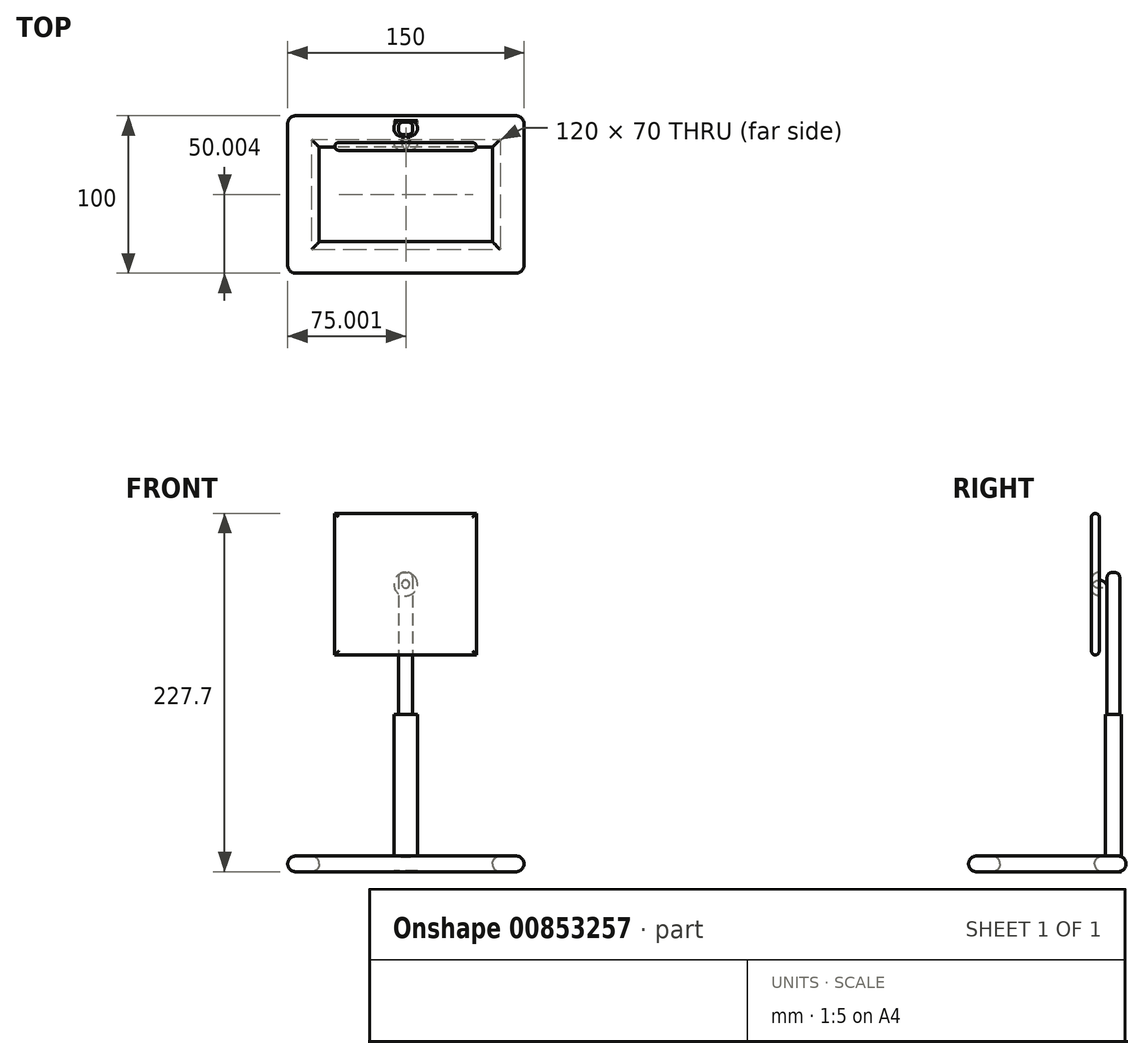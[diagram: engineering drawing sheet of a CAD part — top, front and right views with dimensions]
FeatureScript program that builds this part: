
annotation { "Feature Type Name" : "Feature", "Feature Type Description" : "" }
export const myFeature = defineFeature(function(context is Context, id is Id, definition is map)
    precondition{}
    {
        {
            var Q0;
            Q0=qCreatedBy(makeId("Top.planeOp"),FACE);
            var sketch = newSketch(context, id + "F0", { "sketchPlane" : qUnion([Q0])});
            skLineSegment(sketch, "E0", {"start": v(-74.85, -45.82) * mm, "end": v(75.15, -45.82) * mm});
            skLineSegment(sketch, "E1", {"start": v(-74.85, -45.82) * mm, "end": v(-74.85, 54.18) * mm});
            skLineSegment(sketch, "E2", {"start": v(-74.85, 54.18) * mm, "end": v(75.15, 54.18) * mm});
            skLineSegment(sketch, "E3", {"start": v(75.15, 54.18) * mm, "end": v(75.15, -45.82) * mm});
            skLineSegment(sketch, "E4", {"start": v(-54.85, 34.18) * mm, "end": v(-54.85, -25.82) * mm});
            skLineSegment(sketch, "E5", {"start": v(55.15, 34.18) * mm, "end": v(55.15, -25.82) * mm});
            skLineSegment(sketch, "E6", {"start": v(-54.85, 34.18) * mm, "end": v(55.15, 34.18) * mm});
            skLineSegment(sketch, "E7.trimOffspring", {"start": v(-54.85, -25.82) * mm, "end": v(55.15, -25.82) * mm});
            skLineSegment(sketch, "E8", {"start": v(0, 0) * mm, "end": v(0.15, 111.46) * mm, "construction": true});
            skPoint(sketch, "E8.endSnap0", {"position": v(0.15, 54.18) * mm});
            skLineSegment(sketch, "E9", {"start": v(-7.43, 51.18) * mm, "end": v(7.57, 51.18) * mm});
            skLineSegment(sketch, "E10", {"start": v(-7.43, 51.18) * mm, "end": v(-7.43, 41.18) * mm});
            skLineSegment(sketch, "E11", {"start": v(-7.43, 41.18) * mm, "end": v(7.57, 41.18) * mm});
            skLineSegment(sketch, "E12", {"start": v(7.57, 41.18) * mm, "end": v(7.57, 51.18) * mm});
            skSolve(sketch);
        }
        {
            var Q0;
            Q0=qSketchRegion(id+"F0",true);
            extrude(context, id + "F1", {"entities" : qUnion([Q0]), "depth" : 10 * mm, "offsetDistance" : 25 * mm});
        }
        {
            var Q0;
            Q0=makeQuery(id+"F1.opExtrude","CAP_EDGE",EDGE,{"disambiguationData":[OSD([sQuery(id+"F0.wireOp",EDGE,"E2")])],"isStart":false});
            var Q1;
            Q1=makeQuery(id+"F1.opExtrude","CAP_EDGE",EDGE,{"disambiguationData":[OSD([sQuery(id+"F0.wireOp",EDGE,"E1")])],"isStart":false});
            var Q2;
            Q2=makeQuery(id+"F1.opExtrude","CAP_EDGE",EDGE,{"disambiguationData":[OSD([sQuery(id+"F0.wireOp",EDGE,"E0")])],"isStart":false});
            var Q3;
            Q3=makeQuery(id+"F1.opExtrude","CAP_EDGE",EDGE,{"disambiguationData":[OSD([sQuery(id+"F0.wireOp",EDGE,"E3")])],"isStart":false});
            var Q4;
            Q4=makeQuery(id+"F1.opExtrude","CAP_EDGE",EDGE,{"disambiguationData":[OSD([sQuery(id+"F0.wireOp",EDGE,"E6")])],"isStart":false});
            var Q5;
            Q5=makeQuery(id+"F1.opExtrude","CAP_EDGE",EDGE,{"disambiguationData":[OSD([sQuery(id+"F0.wireOp",EDGE,"E4")])],"isStart":false});
            var Q6;
            Q6=makeQuery(id+"F1.opExtrude","CAP_EDGE",EDGE,{"disambiguationData":[OSD([sQuery(id+"F0.wireOp",EDGE,"E5")])],"isStart":false});
            var Q7;
            Q7=makeQuery(id+"F1.opExtrude","CAP_EDGE",EDGE,{"disambiguationData":[OSD([sQuery(id+"F0.wireOp",EDGE,"E7.trimOffspring")])],"isStart":false});
            fillet(context, id + "F2", {"entities" : qUnion([Q0, Q1, Q2, Q3, Q4, Q5, Q6, Q7]), "radius" : 5 * mm, "tangentPropagation" : true, "allowEdgeOverflow" : false});
        }
        {
            var Q0;
            Q0=makeQuery(id+"F1.opExtrude","CAP_EDGE",EDGE,{"disambiguationData":[OSD([sQuery(id+"F0.wireOp",EDGE,"E0")])],"isStart":true});
            fillet(context, id + "F3", {"entities" : qUnion([Q0]), "radius" : 5 * mm, "tangentPropagation" : true, "allowEdgeOverflow" : false});
        }
        {
            var Q0;
            Q0=makeQuery(id+"F1.opExtrude","CAP_EDGE",EDGE,{"disambiguationData":[OSD([sQuery(id+"F0.wireOp",EDGE,"E2")])],"isStart":true});
            fillet(context, id + "F4", {"entities" : qUnion([Q0]), "radius" : 5 * mm, "tangentPropagation" : true, "allowEdgeOverflow" : false});
        }
        {
            var Q0;
            Q0=makeQuery(id+"F1.opExtrude","CAP_EDGE",EDGE,{"disambiguationData":[OSD([sQuery(id+"F0.wireOp",EDGE,"E5")])],"isStart":true});
            var Q1;
            Q1=makeQuery(id+"F1.opExtrude","CAP_EDGE",EDGE,{"disambiguationData":[OSD([sQuery(id+"F0.wireOp",EDGE,"E6")])],"isStart":true});
            var Q2;
            Q2=makeQuery(id+"F1.opExtrude","CAP_EDGE",EDGE,{"disambiguationData":[OSD([sQuery(id+"F0.wireOp",EDGE,"E7.trimOffspring")])],"isStart":true});
            var Q3;
            Q3=makeQuery(id+"F1.opExtrude","CAP_EDGE",EDGE,{"disambiguationData":[OSD([sQuery(id+"F0.wireOp",EDGE,"E4")])],"isStart":true});
            fillet(context, id + "F5", {"entities" : qUnion([Q0, Q1, Q2, Q3]), "radius" : 5 * mm, "tangentPropagation" : true, "allowEdgeOverflow" : false});
        }
        {
            var Q0;
            Q0=makeQuery(id+"F2.opFillet","BLEND_EDGE",EDGE,{"blendedFrom":[makeQuery(id+"F1.opExtrude","CAP_EDGE",EDGE,{"disambiguationData":[OSD([sQuery(id+"F0.wireOp",EDGE,"E0")])],"isStart":false}),makeQuery(id+"F1.opExtrude","CAP_EDGE",EDGE,{"disambiguationData":[OSD([sQuery(id+"F0.wireOp",EDGE,"E3")])],"isStart":false})],"blendedInto":[]});
            fillet(context, id + "F6", {"entities" : qUnion([Q0]), "radius" : 5 * mm, "tangentPropagation" : true, "allowEdgeOverflow" : false});
        }
        {
            var Q0;
            Q0=makeQuery(id+"F2.opFillet","BLEND_EDGE",EDGE,{"blendedFrom":[makeQuery(id+"F1.opExtrude","CAP_EDGE",EDGE,{"disambiguationData":[OSD([sQuery(id+"F0.wireOp",EDGE,"E1")])],"isStart":false}),makeQuery(id+"F1.opExtrude","CAP_EDGE",EDGE,{"disambiguationData":[OSD([sQuery(id+"F0.wireOp",EDGE,"E2")])],"isStart":false})],"blendedInto":[]});
            fillet(context, id + "F7", {"entities" : qUnion([Q0]), "radius" : 5 * mm, "tangentPropagation" : true, "allowEdgeOverflow" : false});
        }
        {
            var Q0;
            Q0=makeQuery(id+"F0.imprint","IMPRINT",FACE,{"disambiguationData":[TD([[makeQuery(id+"F0.imprint","IMPRINT",EDGE,{"derivedFrom":sQuery(id+"F0.wireOp",EDGE,"E9")}),-1.0]])]});
            extrude(context, id + "F8", {"entities" : qUnion([Q0]), "operationType" : NewBodyOperationType.ADD, "depth" : 100 * mm, "offsetDistance" : 25 * mm});
        }
        {
            var Q0;
            Q0=makeQuery(id+"F8.opExtrude","SWEPT_EDGE",EDGE,{"disambiguationData":[OSD([sQuery(id+"F0.wireOp",EDGE,"E11"),sQuery(id+"F0.wireOp",EDGE,"E12")])]});
            var Q1;
            {var subQ0=sQuery(id+"F0.wireOp",EDGE,"E9");var subQ1=sQuery(id+"F0.wireOp",EDGE,"E12");Q1=makeQuery(id+"F8.boolean.opBoolean","SPLIT",EDGE,{"disambiguationData":[TD([makeQuery(id+"F8.opExtrude","CAP_FACE",FACE,{"disambiguationData":[OSD([subQ0,sQuery(id+"F0.wireOp",EDGE,"E10"),sQuery(id+"F0.wireOp",EDGE,"E11"),subQ1])],"isStart":false})])],"derivedFrom":makeQuery(id+"F8.opExtrude","SWEPT_EDGE",EDGE,{"disambiguationData":[OSD([subQ0,subQ1])]})});}
            var Q2;
            Q2=makeQuery(id+"F8.opExtrude","SWEPT_EDGE",EDGE,{"disambiguationData":[OSD([sQuery(id+"F0.wireOp",EDGE,"E10"),sQuery(id+"F0.wireOp",EDGE,"E11")])]});
            var Q3;
            {var subQ0=sQuery(id+"F0.wireOp",EDGE,"E9");var subQ1=sQuery(id+"F0.wireOp",EDGE,"E10");Q3=makeQuery(id+"F8.boolean.opBoolean","SPLIT",EDGE,{"disambiguationData":[TD([makeQuery(id+"F8.opExtrude","CAP_FACE",FACE,{"disambiguationData":[OSD([subQ0,subQ1,sQuery(id+"F0.wireOp",EDGE,"E11"),sQuery(id+"F0.wireOp",EDGE,"E12")])],"isStart":false})])],"derivedFrom":makeQuery(id+"F8.opExtrude","SWEPT_EDGE",EDGE,{"disambiguationData":[OSD([subQ0,subQ1])]})});}
            fillet(context, id + "F9", {"entities" : qUnion([Q0, Q1, Q2, Q3]), "radius" : 5 * mm, "tangentPropagation" : true, "allowEdgeOverflow" : false});
        }
        {
            var Q0;
            Q0=makeQuery(id+"F8.opExtrude","CAP_FACE",FACE,{"disambiguationData":[OSD([sQuery(id+"F0.wireOp",EDGE,"E9"),sQuery(id+"F0.wireOp",EDGE,"E10"),sQuery(id+"F0.wireOp",EDGE,"E11"),sQuery(id+"F0.wireOp",EDGE,"E12")])],"isStart":false});
            var sketch = newSketch(context, id + "F10", { "sketchPlane" : qUnion([Q0])});
            skLineSegment(sketch, "E13", {"start": v(-4.5, 42.18) * mm, "end": v(4.5, 42.18) * mm});
            skLineSegment(sketch, "E14", {"start": v(4.5, 42.18) * mm, "end": v(4.5, 50.18) * mm});
            skLineSegment(sketch, "E15", {"start": v(-4.5, 50.18) * mm, "end": v(4.5, 50.18) * mm});
            skLineSegment(sketch, "E16", {"start": v(-4.5, 50.18) * mm, "end": v(-4.5, 42.18) * mm});
            skLineSegment(sketch, "E17", {"start": v(0, 42.18) * mm, "end": v(0, 55.6) * mm, "construction": true});
            skSolve(sketch);
        }
        {
            var Q0;
            {var subQ1=sQuery(id+"F0.wireOp",EDGE,"E12");var subQ2=sQuery(id+"F0.wireOp",EDGE,"E11");var subQ3=sQuery(id+"F0.wireOp",EDGE,"E10");var subQ4=makeQuery(id+"F8.opExtrude","CAP_FACE",FACE,{"disambiguationData":[OSD([sQuery(id+"F0.wireOp",EDGE,"E9"),subQ3,subQ2,subQ1])],"isStart":false});var subQ5=makeQuery(id+"F9.opFillet","BLEND_EDGE",EDGE,{"blendedFrom":[makeQuery(id+"F8.opExtrude","SWEPT_EDGE",EDGE,{"disambiguationData":[OSD([subQ3,subQ2])]}),subQ4],"blendedInto":[subQ4]});var subQ15=sQuery(id+"F10.wireOp",EDGE,"E13");var subQ16=makeQuery(id+"F10.imprint","INTERSECT",VERTEX,{"derivedFrom":[subQ5,subQ15]});Q0=makeQuery(id+"F10.imprint","IMPRINT",FACE,{"disambiguationData":[TD([[makeQuery(id+"F10.imprint","IMPRINT",EDGE,{"disambiguationData":[TD([[subQ16,-1.0]])],"derivedFrom":subQ15}),1.0]])]});}
            extrude(context, id + "F11", {"entities" : qUnion([Q0]), "operationType" : NewBodyOperationType.ADD, "depth" : 90 * mm, "offsetDistance" : 25 * mm});
        }
        {
            var Q0;
            {var subQ0=sQuery(id+"F10.wireOp",EDGE,"E14");var subQ1=sQuery(id+"F0.wireOp",EDGE,"E12");var subQ2=sQuery(id+"F0.wireOp",EDGE,"E11");var subQ3=sQuery(id+"F0.wireOp",EDGE,"E10");var subQ4=sQuery(id+"F0.wireOp",EDGE,"E9");Q0=makeQuery(id+"F11.opExtrude","SWEPT_EDGE",EDGE,{"disambiguationData":[OSD([subQ4,subQ3,subQ2,subQ1,subQ0]),TDD([makeQuery(id+"F10.imprint","INTERSECT",VERTEX,{"disambiguationData":[OD(0.0)],"derivedFrom":[makeQuery(id+"F9.opFillet","BLEND_EDGE",EDGE,{"blendedFrom":[makeQuery(id+"F8.opExtrude","SWEPT_EDGE",EDGE,{"disambiguationData":[OSD([subQ2,subQ1])]}),makeQuery(id+"F8.opExtrude","CAP_FACE",FACE,{"disambiguationData":[OSD([subQ4,subQ3,subQ2,subQ1])],"isStart":false})],"blendedInto":[makeQuery(id+"F8.opExtrude","CAP_FACE",FACE,{"disambiguationData":[OSD([subQ4,subQ3,subQ2,subQ1])],"isStart":false})]}),subQ0]})])]});}
            var Q1;
            {var subQ0=sQuery(id+"F10.wireOp",EDGE,"E14");var subQ1=sQuery(id+"F0.wireOp",EDGE,"E12");var subQ2=sQuery(id+"F0.wireOp",EDGE,"E11");var subQ3=sQuery(id+"F0.wireOp",EDGE,"E10");var subQ4=sQuery(id+"F0.wireOp",EDGE,"E9");Q1=makeQuery(id+"F11.opExtrude","SWEPT_EDGE",EDGE,{"disambiguationData":[OSD([subQ4,subQ3,subQ2,subQ1,subQ0]),TDD([makeQuery(id+"F10.imprint","INTERSECT",VERTEX,{"disambiguationData":[OD(1.0)],"derivedFrom":[makeQuery(id+"F9.opFillet","BLEND_EDGE",EDGE,{"blendedFrom":[makeQuery(id+"F8.opExtrude","SWEPT_EDGE",EDGE,{"disambiguationData":[OSD([subQ2,subQ1])]}),makeQuery(id+"F8.opExtrude","CAP_FACE",FACE,{"disambiguationData":[OSD([subQ4,subQ3,subQ2,subQ1])],"isStart":false})],"blendedInto":[makeQuery(id+"F8.opExtrude","CAP_FACE",FACE,{"disambiguationData":[OSD([subQ4,subQ3,subQ2,subQ1])],"isStart":false})]}),subQ0]})])]});}
            fillet(context, id + "F12", {"entities" : qUnion([Q0, Q1]), "radius" : 3 * mm, "tangentPropagation" : true, "allowEdgeOverflow" : false});
        }
        {
            var Q0;
            {var subQ0=sQuery(id+"F10.wireOp",EDGE,"E16");var subQ1=sQuery(id+"F0.wireOp",EDGE,"E12");var subQ2=sQuery(id+"F0.wireOp",EDGE,"E11");var subQ3=sQuery(id+"F0.wireOp",EDGE,"E10");var subQ4=sQuery(id+"F0.wireOp",EDGE,"E9");Q0=makeQuery(id+"F11.opExtrude","SWEPT_EDGE",EDGE,{"disambiguationData":[OSD([subQ4,subQ3,subQ2,subQ1,subQ0]),TDD([makeQuery(id+"F10.imprint","INTERSECT",VERTEX,{"disambiguationData":[OD(1.0)],"derivedFrom":[makeQuery(id+"F9.opFillet","BLEND_EDGE",EDGE,{"blendedFrom":[makeQuery(id+"F8.opExtrude","SWEPT_EDGE",EDGE,{"disambiguationData":[OSD([subQ3,subQ2])]}),makeQuery(id+"F8.opExtrude","CAP_FACE",FACE,{"disambiguationData":[OSD([subQ4,subQ3,subQ2,subQ1])],"isStart":false})],"blendedInto":[makeQuery(id+"F8.opExtrude","CAP_FACE",FACE,{"disambiguationData":[OSD([subQ4,subQ3,subQ2,subQ1])],"isStart":false})]}),subQ0]})])]});}
            var Q1;
            {var subQ0=sQuery(id+"F10.wireOp",EDGE,"E16");var subQ1=sQuery(id+"F0.wireOp",EDGE,"E12");var subQ2=sQuery(id+"F0.wireOp",EDGE,"E11");var subQ3=sQuery(id+"F0.wireOp",EDGE,"E10");var subQ4=sQuery(id+"F0.wireOp",EDGE,"E9");Q1=makeQuery(id+"F11.opExtrude","SWEPT_EDGE",EDGE,{"disambiguationData":[OSD([subQ4,subQ3,subQ2,subQ1,subQ0]),TDD([makeQuery(id+"F10.imprint","INTERSECT",VERTEX,{"disambiguationData":[OD(0.0)],"derivedFrom":[makeQuery(id+"F9.opFillet","BLEND_EDGE",EDGE,{"blendedFrom":[makeQuery(id+"F8.opExtrude","SWEPT_EDGE",EDGE,{"disambiguationData":[OSD([subQ3,subQ2])]}),makeQuery(id+"F8.opExtrude","CAP_FACE",FACE,{"disambiguationData":[OSD([subQ4,subQ3,subQ2,subQ1])],"isStart":false})],"blendedInto":[makeQuery(id+"F8.opExtrude","CAP_FACE",FACE,{"disambiguationData":[OSD([subQ4,subQ3,subQ2,subQ1])],"isStart":false})]}),subQ0]})])]});}
            fillet(context, id + "F13", {"entities" : qUnion([Q0, Q1]), "radius" : 3 * mm, "tangentPropagation" : true, "allowEdgeOverflow" : false});
        }
        {
            var Q0;
            Q0=makeQuery(id+"F11.opExtrude","CAP_EDGE",EDGE,{"disambiguationData":[OSD([sQuery(id+"F10.wireOp",EDGE,"E13")])],"isStart":false});
            var Q1;
            Q1=makeQuery(id+"F11.opExtrude","CAP_EDGE",EDGE,{"disambiguationData":[OSD([sQuery(id+"F10.wireOp",EDGE,"E15")])],"isStart":false});
            fillet(context, id + "F14", {"entities" : qUnion([Q0, Q1]), "radius" : 3 * mm, "tangentPropagation" : true, "allowEdgeOverflow" : false});
        }
        {
            var Q0;
            Q0=makeQuery(id+"F11.opExtrude","SWEPT_FACE",FACE,{"disambiguationData":[OSD([sQuery(id+"F10.wireOp",EDGE,"E13")])]});
            var sketch = newSketch(context, id + "F15", { "sketchPlane" : qUnion([Q0])});
            skLineSegment(sketch, "E18", {"start": v(0, 0) * mm, "end": v(0, 194.28) * mm, "construction": true});
            skCircle(sketch, "E19", {"center": v(0, 182.7) * mm, "radius": 7.5 * mm});
            skSolve(sketch);
        }
        {
            var Q0;
            Q0 = qSketchRegion(id + "F15", true);
            extrude(context, id + "F16", {"entities" : qUnion([Q0]), "depth" : 5 * mm, "offsetDistance" : 25 * mm});
        }
        {
            var Q0;
            Q0=makeQuery(id+"F16.opExtrude","CAP_FACE",FACE,{"disambiguationData":[OSD([sQuery(id+"F15.wireOp",EDGE,"E19")])],"isStart":false});
            var sketch = newSketch(context, id + "F17", { "sketchPlane" : qUnion([Q0])});
            skLineSegment(sketch, "E20", {"start": v(-45, 137.7) * mm, "end": v(-45, 227.7) * mm});
            skLineSegment(sketch, "E21", {"start": v(-45, 227.7) * mm, "end": v(45, 227.7) * mm});
            skLineSegment(sketch, "E22", {"start": v(45, 227.7) * mm, "end": v(45, 137.7) * mm});
            skLineSegment(sketch, "E23", {"start": v(45, 137.7) * mm, "end": v(-45, 137.7) * mm});
            skLineSegment(sketch, "E24", {"start": v(0, 182.7) * mm, "end": v(-85.96, 182.7) * mm, "construction": true});
            skSolve(sketch);
        }
        {
            var Q0;
            Q0 = qSketchRegion(id + "F17", true);
            extrude(context, id + "F18", {"entities" : qUnion([Q0]), "operationType" : NewBodyOperationType.ADD, "depth" : 5 * mm, "offsetDistance" : 25 * mm});
        }
        {
            var Q0;
            Q0=makeQuery(id+"F18.opExtrude","CAP_EDGE",EDGE,{"disambiguationData":[OSD([sQuery(id+"F17.wireOp",EDGE,"E21")])],"isStart":false});
            var Q1;
            Q1=makeQuery(id+"F18.opExtrude","CAP_EDGE",EDGE,{"disambiguationData":[OSD([sQuery(id+"F17.wireOp",EDGE,"E21")])],"isStart":true});
            var Q2;
            Q2=makeQuery(id+"F18.opExtrude","CAP_EDGE",EDGE,{"disambiguationData":[OSD([sQuery(id+"F17.wireOp",EDGE,"E22")])],"isStart":false});
            var Q3;
            Q3=makeQuery(id+"F18.opExtrude","CAP_EDGE",EDGE,{"disambiguationData":[OSD([sQuery(id+"F17.wireOp",EDGE,"E22")])],"isStart":true});
            var Q4;
            Q4=makeQuery(id+"F18.opExtrude","CAP_EDGE",EDGE,{"disambiguationData":[OSD([sQuery(id+"F17.wireOp",EDGE,"E20")])],"isStart":false});
            var Q5;
            Q5=makeQuery(id+"F18.opExtrude","CAP_EDGE",EDGE,{"disambiguationData":[OSD([sQuery(id+"F17.wireOp",EDGE,"E20")])],"isStart":true});
            var Q6;
            Q6=makeQuery(id+"F18.opExtrude","CAP_EDGE",EDGE,{"disambiguationData":[OSD([sQuery(id+"F17.wireOp",EDGE,"E23")])],"isStart":false});
            var Q7;
            Q7=makeQuery(id+"F18.opExtrude","CAP_EDGE",EDGE,{"disambiguationData":[OSD([sQuery(id+"F17.wireOp",EDGE,"E23")])],"isStart":true});
            fillet(context, id + "F19", {"entities" : qUnion([Q0, Q1, Q2, Q3, Q4, Q5, Q6, Q7]), "radius" : 2.5 * mm, "tangentPropagation" : true, "allowEdgeOverflow" : false});
        }
        {
            var Q0;
            Q0=makeQuery(id+"F16.opExtrude","CAP_EDGE",EDGE,{"disambiguationData":[OSD([sQuery(id+"F15.wireOp",EDGE,"E19")])],"isStart":true});
            fillet(context, id + "F20", {"entities" : qUnion([Q0]), "radius" : 5 * mm, "tangentPropagation" : true, "allowEdgeOverflow" : false});
        }
    });
